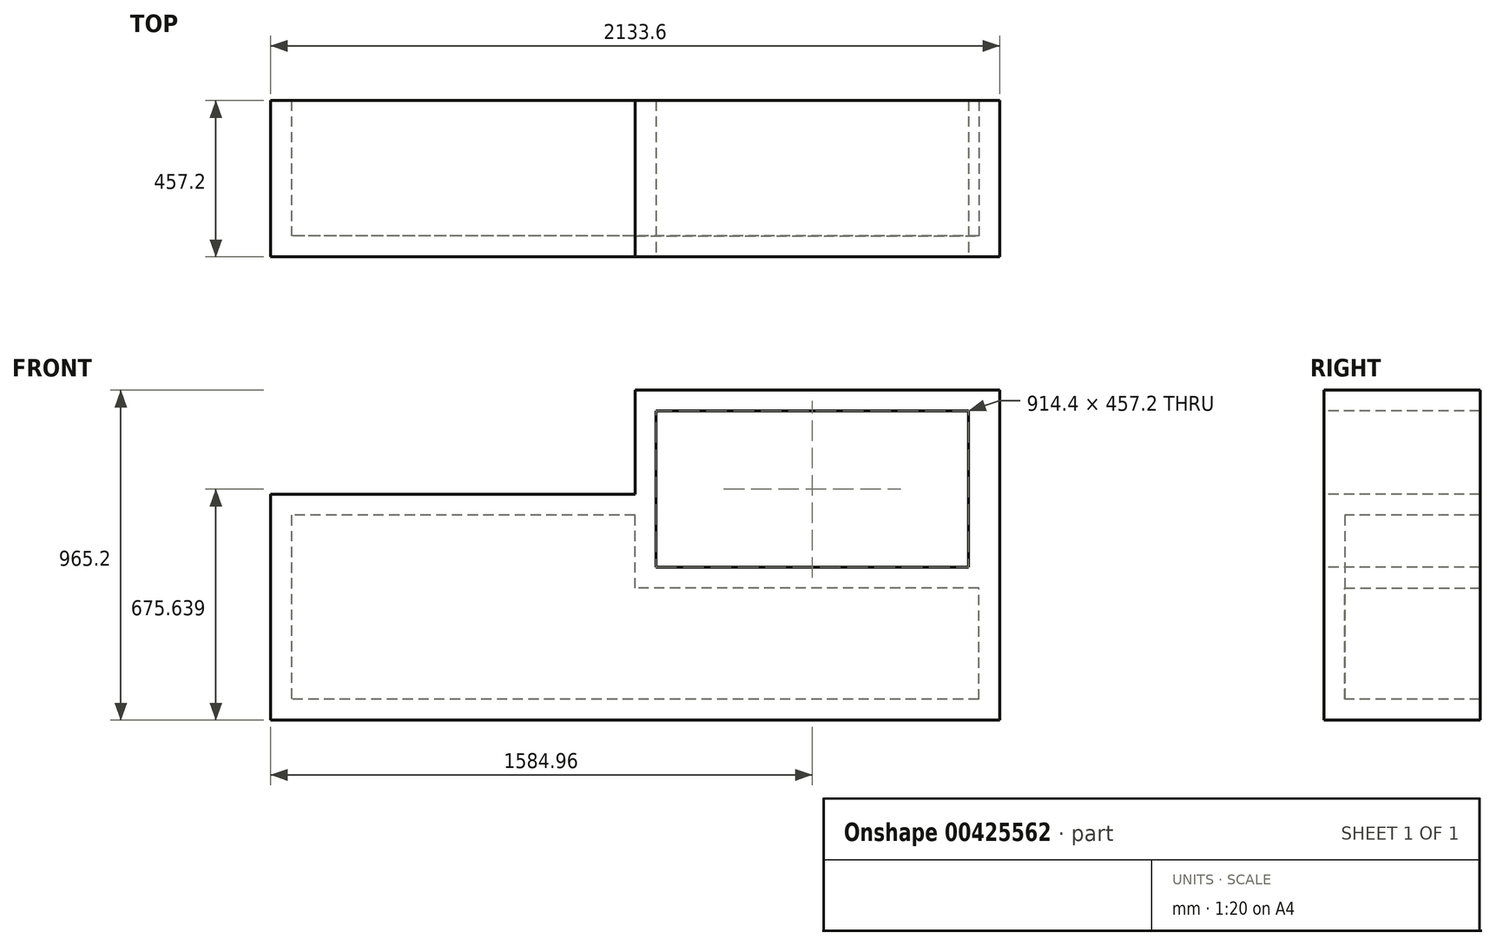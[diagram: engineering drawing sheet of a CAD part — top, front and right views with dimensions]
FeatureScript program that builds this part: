
annotation { "Feature Type Name" : "Feature", "Feature Type Description" : "" }
export const myFeature = defineFeature(function(context is Context, id is Id, definition is map)
    precondition{}
    {
        {
            var Q0;
            Q0=qCreatedBy(makeId("Front.planeOp"),FACE);
            var sketch = newSketch(context, id + "F0", { "sketchPlane" : qUnion([Q0])});
            skLineSegment(sketch, "E0.bottom", {"start": v(-0.05, 0) * mm, "end": v(-1066.85, 0) * mm});
            skLineSegment(sketch, "E0.top", {"start": v(-0.05, -660.4) * mm, "end": v(-1066.85, -660.4) * mm});
            skLineSegment(sketch, "E0.right", {"start": v(-1066.85, 0) * mm, "end": v(-1066.85, -660.4) * mm});
            skLineSegment(sketch, "E1.bottom", {"start": v(-0.05, -660.4) * mm, "end": v(1066.75, -660.4) * mm});
            skLineSegment(sketch, "E1.top", {"start": v(-0.05, 304.8) * mm, "end": v(1066.75, 304.8) * mm});
            skLineSegment(sketch, "E1.left", {"start": v(-0.05, 0) * mm, "end": v(-0.05, 304.8) * mm});
            skLineSegment(sketch, "E1.right", {"start": v(1066.75, -660.4) * mm, "end": v(1066.75, 304.8) * mm});
            skSolve(sketch);
        }
        {
            var Q0;
            Q0=makeQuery(id+"F0.imprint","IMPRINT",FACE,{"disambiguationData":[TD([[makeQuery(id+"F0.imprint","IMPRINT",EDGE,{"derivedFrom":sQuery(id+"F0.wireOp",EDGE,"E0.bottom")}),1.0]])]});
            extrude(context, id + "F1", {"entities" : qUnion([Q0]), "oppositeDirection" : true, "depth" : 457.2 * mm});
        }
        {
            var Q0;
            Q0=makeQuery(id+"F1.opExtrude","CAP_FACE",FACE,{"disambiguationData":[OSD([sQuery(id+"F0.wireOp",EDGE,"E0.bottom"),sQuery(id+"F0.wireOp",EDGE,"E0.top"),sQuery(id+"F0.wireOp",EDGE,"E0.right"),sQuery(id+"F0.wireOp",EDGE,"E1.bottom"),sQuery(id+"F0.wireOp",EDGE,"E1.top"),sQuery(id+"F0.wireOp",EDGE,"E1.left"),sQuery(id+"F0.wireOp",EDGE,"E1.right")])],"isStart":true});
            var sketch = newSketch(context, id + "F2", { "sketchPlane" : qUnion([Q0])});
            skLineSegment(sketch, "E2.bottom", {"start": v(60.9, 243.84) * mm, "end": v(975.3, 243.84) * mm});
            skLineSegment(sketch, "E2.top", {"start": v(60.9, -213.36) * mm, "end": v(975.3, -213.36) * mm});
            skLineSegment(sketch, "E2.left", {"start": v(60.9, 243.84) * mm, "end": v(60.9, -213.36) * mm});
            skLineSegment(sketch, "E2.right", {"start": v(975.3, 243.84) * mm, "end": v(975.3, -213.36) * mm});
            skSolve(sketch);
        }
        {
            var Q0;
            Q0 = qSketchRegion(id + "F2", true);
            extrude(context, id + "F3", {"entities" : qUnion([Q0]), "operationType" : NewBodyOperationType.REMOVE, "endBound" : BoundingType.UP_TO_NEXT, "oppositeDirection" : true, "depth" : 30.48 * mm});
        }
        {
            var Q0;
            Q0=makeQuery(id+"F1.opExtrude","CAP_FACE",FACE,{"disambiguationData":[OSD([sQuery(id+"F0.wireOp",EDGE,"E0.bottom"),sQuery(id+"F0.wireOp",EDGE,"E0.top"),sQuery(id+"F0.wireOp",EDGE,"E0.right"),sQuery(id+"F0.wireOp",EDGE,"E1.bottom"),sQuery(id+"F0.wireOp",EDGE,"E1.top"),sQuery(id+"F0.wireOp",EDGE,"E1.left"),sQuery(id+"F0.wireOp",EDGE,"E1.right")])],"isStart":false});
            shell(context, id + "F4", {"entities" : qUnion([Q0]), "thickness" : 60.96 * mm});
        }
    });
